# Revit family: Faucet-Lavatory-KOHLER-Taut-K-74026BR_1
name_source: partatom
category: Plumbing Fixtures
units: mm (PartAtom-declared; Revit-internal decimal feet)

## family parameters
Cut with Voids When Loaded = No
Host = Face
Maintain Annotation Orientation = No
OmniClass Number = 23.31.11.00
OmniClass Title = Faucets
Part Type = Normal
Room Calculation Point = No
Round Connector Dimension = Use Diameter
Shared = No

## types (3) — shared parameters
ADA Compliant = No
Assembly Code = D2010
CW Connection = Yes
Cold Water Inlet = Cold Water Inlet
Date Modified = 07/19/2022
Default Elevation = 36"
Description = Single Control Tall Lavatory Faucet Without Drain
Drain Included = No
Flow Rate = 2 GPM
HW Connection = Yes
Handle Clearance = 3 1/8"
Hot Water Inlet = Hot Water Inlet
Length = 4 3/4"
Manufacturer = KOHLER Co.
Master Format 2014 = 22 41 39
Master Format 2014 Name = Residential Faucets, Supplies, and Trim
Material = Premium Metal Construction
Product Name = TAUT
Spout Reach = 4 3/4"
URL = https://br.kohler.com
Vent Connection = No
Waste Connection = No
Waste Water Outlet = Waste Water Outlet
WaterSense Certified = No

## per-type parameters (varying)
| type | 4ND | B4ND | Escutcheon Height | Escutcheon Plate | Finish | Height | Model | Pressure | Product Page URL | Secondary Material | Spout Height | Type | Width |
| Without Escutcheon Plate, CP-Polished Chrome | Yes | No | 0" | No | Kohler-Metal-CP-Polished_Chrome | 10 9/16" | K-74026BR-4ND-CP | 43.51 psi |  | Kohler-Plastic-58-Thunder_Grey | 7 7/8" | 1 | 1 7/8" |
| With Escutcheon Plate, BL-Matte Black | No | Yes | 3/16" | Yes | Kohler-Metal-BL-Matte_Black | 10 3/4" | K-74026BR-B4ND-BL | 60.05 psi | https://br.kohler.com | Kohler-Plastic-7-Black_Black | 8 1/16" | 3 | 2 3/16" |
| With Escutcheon Plate, CP-Polished Chrome | No | Yes | 3/16" | Yes | Kohler-Metal-CP-Polished_Chrome | 10 3/4" | K-74026BR-B4ND-CP | 60.05 psi |  | Kohler-Plastic-7-Black_Black | 8 1/16" | 2 | 2 3/16" |

## geometry (parser evidence)
native form markers: Sweep x8
no freeform markers — native parametric forms only
